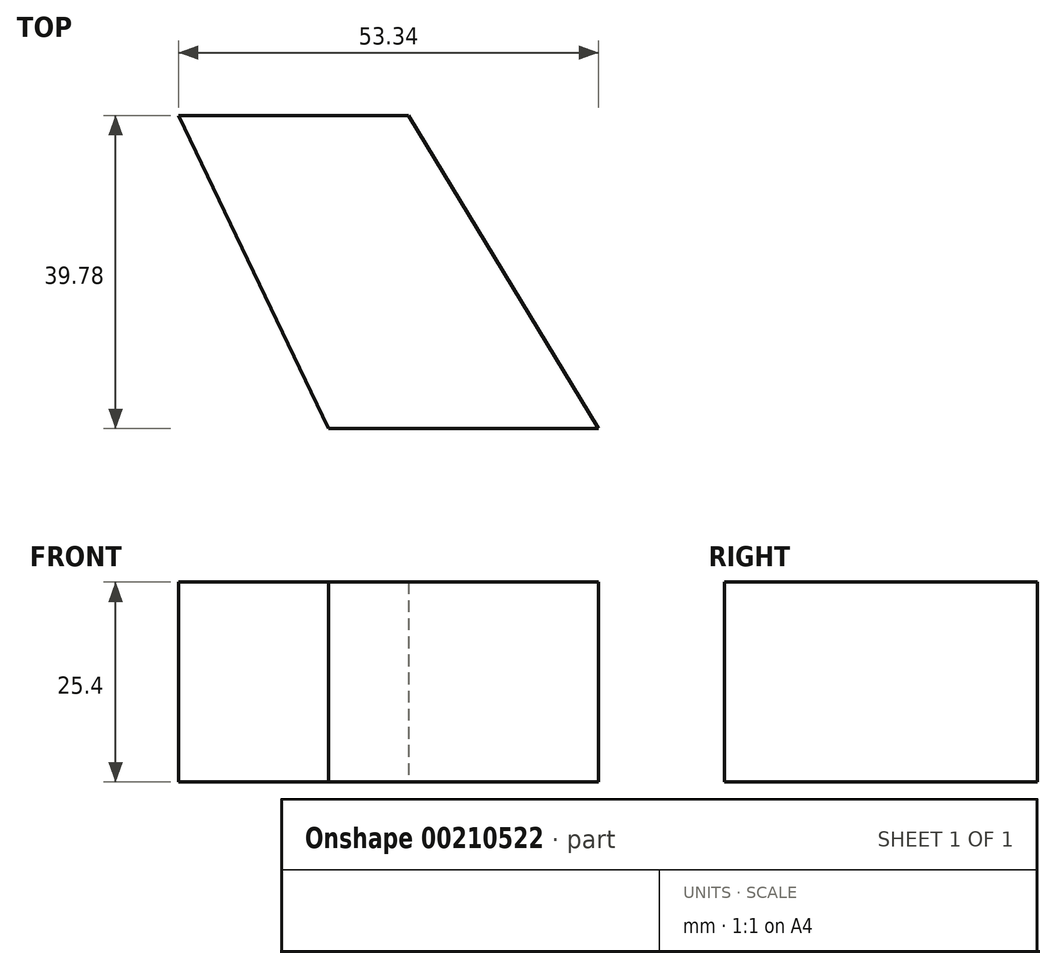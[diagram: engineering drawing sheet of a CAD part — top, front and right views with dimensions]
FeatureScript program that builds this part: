
annotation { "Feature Type Name" : "Feature", "Feature Type Description" : "" }
export const myFeature = defineFeature(function(context is Context, id is Id, definition is map)
    precondition{}
    {
        {
            var Q0;
            Q0=qCreatedBy(makeId("Top.planeOp"),FACE);
            var sketch = newSketch(context, id + "F0", { "sketchPlane" : qUnion([Q0])});
            skLineSegment(sketch, "E0", {"start": v(-18.48, 0) * mm, "end": v(15.8, 0) * mm});
            skLineSegment(sketch, "E1", {"start": v(15.8, 0) * mm, "end": v(-8.34, 39.78) * mm});
            skLineSegment(sketch, "E2", {"start": v(-18.48, 0) * mm, "end": v(-37.55, 39.78) * mm});
            skLineSegment(sketch, "E3", {"start": v(-8.34, 39.78) * mm, "end": v(-37.55, 39.78) * mm});
            skSolve(sketch);
        }
        {
            var Q0;
            Q0=makeQuery(id+"F0.imprint","IMPRINT",FACE,{"disambiguationData":[TD([[makeQuery(id+"F0.imprint","IMPRINT",EDGE,{"derivedFrom":sQuery(id+"F0.wireOp",EDGE,"E0")}),1.0]])]});
            extrude(context, id + "F1", {"entities" : qUnion([Q0]), "depth" : 25.4 * mm});
        }
    });
